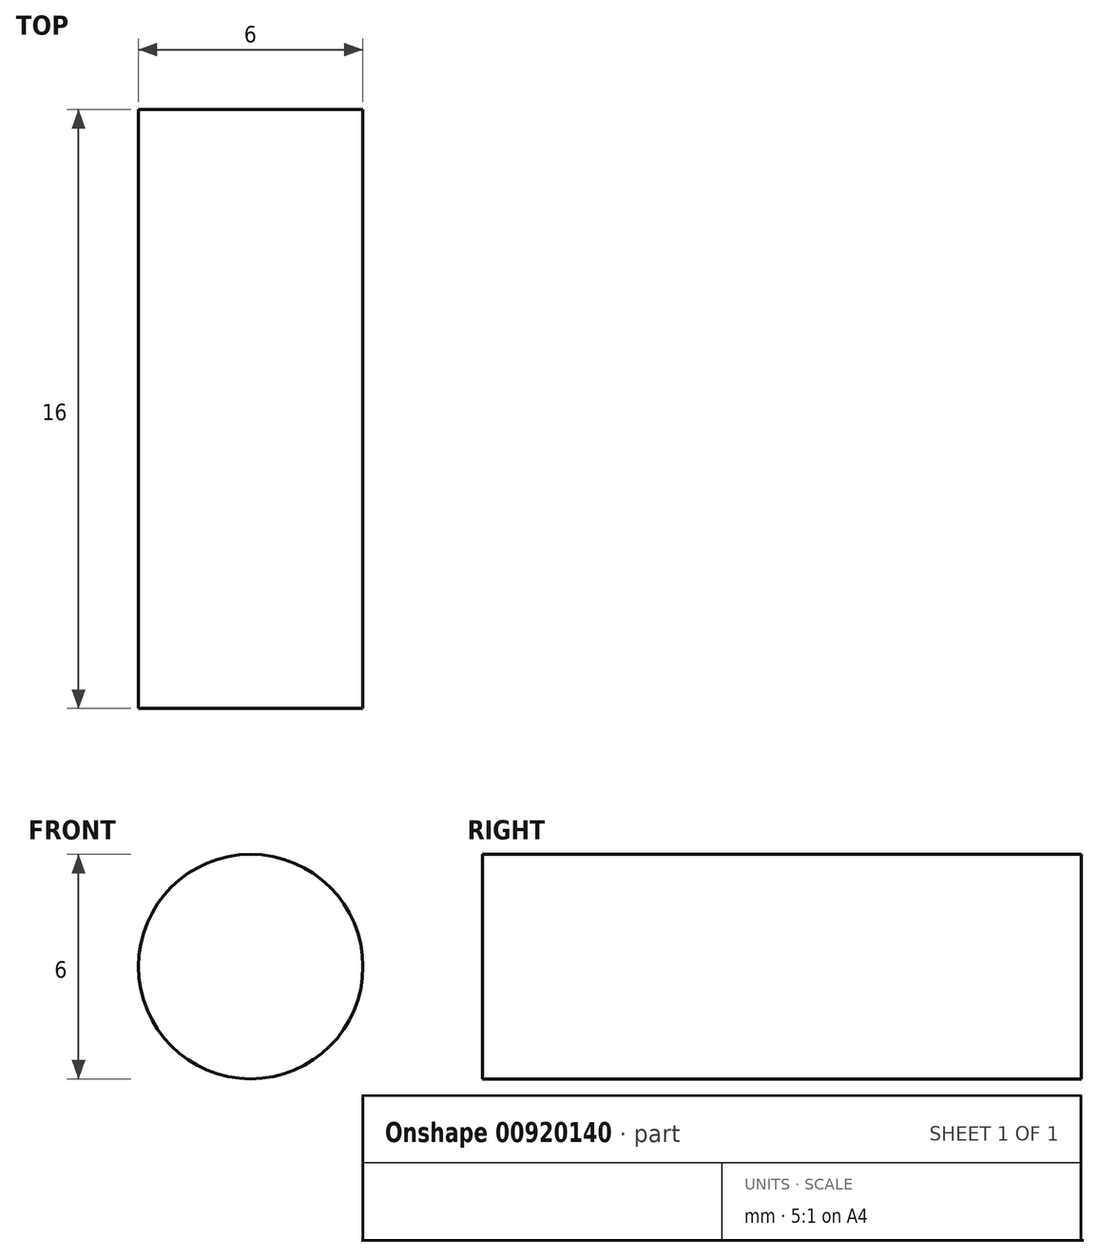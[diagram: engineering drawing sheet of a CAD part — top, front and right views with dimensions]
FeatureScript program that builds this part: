
annotation { "Feature Type Name" : "Feature", "Feature Type Description" : "" }
export const myFeature = defineFeature(function(context is Context, id is Id, definition is map)
    precondition{}
    {
        {
            var Q0;
            Q0=qCreatedBy(makeId("Front.planeOp"),FACE);
            var sketch = newSketch(context, id + "F0", { "sketchPlane" : qUnion([Q0])});
            skCircle(sketch, "E0", {"center": v(0, 0) * mm, "radius": 3 * mm});
            skSolve(sketch);
        }
        {
            var Q0;
            Q0 = qSketchRegion(id + "F0", true);
            extrude(context, id + "F1", {"entities" : qUnion([Q0]), "depth" : 16 * mm, "offsetDistance" : 25 * mm});
        }
    });
